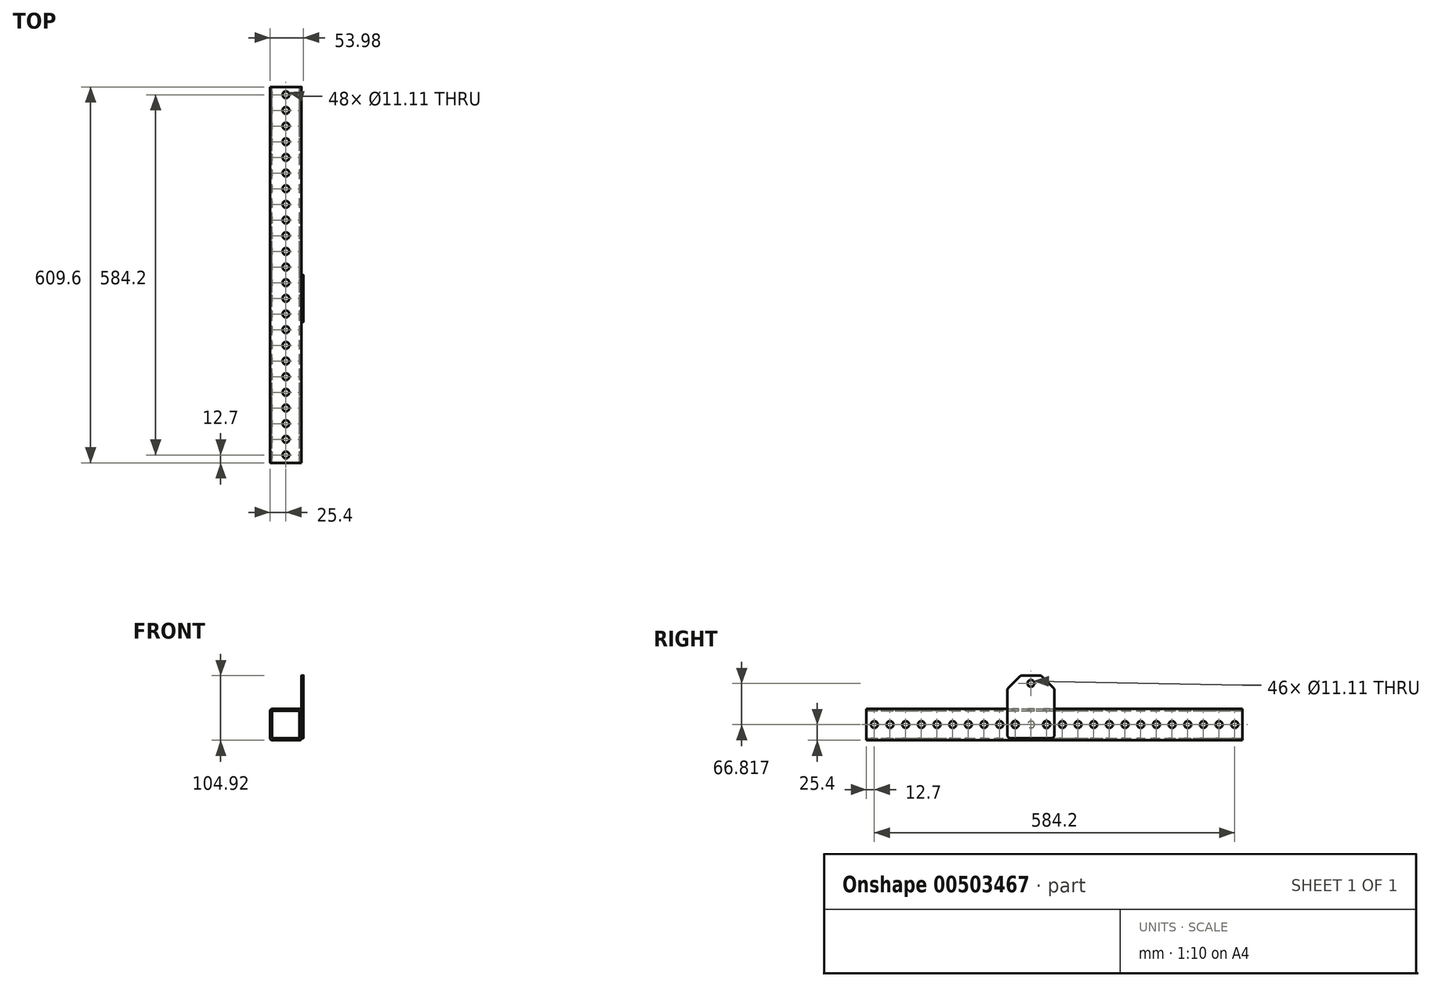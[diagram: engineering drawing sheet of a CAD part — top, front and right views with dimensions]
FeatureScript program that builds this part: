
annotation { "Feature Type Name" : "Feature", "Feature Type Description" : "" }
export const myFeature = defineFeature(function(context is Context, id is Id, definition is map)
    precondition{}
    {
        {
            var Q0;
            Q0=qCreatedBy(makeId("Front.planeOp"),FACE);
            var sketch = newSketch(context, id + "F0", { "sketchPlane" : qUnion([Q0])});
            skLineSegment(sketch, "E0.bottom", {"start": v(-3.18, 0) * mm, "end": v(-47.63, 0) * mm});
            skLineSegment(sketch, "E0.top", {"start": v(-3.17, 50.8) * mm, "end": v(-47.63, 50.8) * mm});
            skLineSegment(sketch, "E0.left", {"start": v(0, 3.18) * mm, "end": v(0, 47.63) * mm});
            skLineSegment(sketch, "E0.right", {"start": v(-50.8, 3.17) * mm, "end": v(-50.8, 47.62) * mm});
            skPoint(sketch, "E1.visualSharp", {"position": v(-50.8, 50.8) * mm});
            skArc(sketch, "E1.filletArc", {"start": v(-47.63, 50.8) * mm, "mid": v(-49.87, 49.87) * mm, "end": v(-50.8, 47.62) * mm});
            skPoint(sketch, "E2.visualSharp", {"position": v(0, 50.8) * mm});
            skArc(sketch, "E2.filletArc", {"start": v(0, 47.63) * mm, "mid": v(-0.93, 49.87) * mm, "end": v(-3.17, 50.8) * mm});
            skPoint(sketch, "E3.visualSharp", {"position": v(0, 0) * mm});
            skArc(sketch, "E3.filletArc", {"start": v(-3.18, 0) * mm, "mid": v(-0.93, 0.93) * mm, "end": v(0, 3.18) * mm});
            skPoint(sketch, "E4.visualSharp", {"position": v(-50.8, 0) * mm});
            skArc(sketch, "E4.filletArc", {"start": v(-50.8, 3.17) * mm, "mid": v(-49.87, 0.93) * mm, "end": v(-47.63, 0) * mm});
            skLineSegment(sketch, "E5.0", {"start": v(-3.18, 3.18) * mm, "end": v(-47.62, 3.17) * mm});
            skLineSegment(sketch, "E5.1", {"start": v(-3.18, 3.18) * mm, "end": v(-3.18, 47.63) * mm});
            skLineSegment(sketch, "E5.2", {"start": v(-3.18, 47.63) * mm, "end": v(-47.63, 47.62) * mm});
            skLineSegment(sketch, "E5.3", {"start": v(-47.62, 3.17) * mm, "end": v(-47.63, 47.62) * mm});
            skSolve(sketch);
        }
        {
            var Q0;
            Q0=makeQuery(id+"F0.imprint","IMPRINT",FACE,{"disambiguationData":[TD([[makeQuery(id+"F0.imprint","IMPRINT",EDGE,{"derivedFrom":sQuery(id+"F0.wireOp",EDGE,"E0.bottom")}),-1.0]])]});
            extrude(context, id + "F1", {"entities" : qUnion([Q0]), "depth" : 609.6 * mm, "offsetDistance" : 25.4 * mm, "symmetric" : true});
        }
        {
            var Q0;
            Q0=makeQuery(id+"F1.opExtrude","SWEPT_FACE",FACE,{"disambiguationData":[OSD([sQuery(id+"F0.wireOp",EDGE,"E0.right")])]});
            var sketch = newSketch(context, id + "F2", { "sketchPlane" : qUnion([Q0])});
            skLineSegment(sketch, "E6", {"start": v(-292.1, 3.17) * mm, "end": v(-292.1, 47.63) * mm, "construction": true});
            skLineSegment(sketch, "E7", {"start": v(-304.8, 25.4) * mm, "end": v(-292.1, 25.4) * mm, "construction": true});
            skCircle(sketch, "E8", {"center": v(-292.1, 25.4) * mm, "radius": 5.56 * mm});
            skCircle(sketch, "E9.1.0.0", {"center": v(-266.7, 25.4) * mm, "radius": 5.56 * mm});
            skCircle(sketch, "E9.2.0.0", {"center": v(-241.3, 25.4) * mm, "radius": 5.56 * mm});
            skCircle(sketch, "E9.3.0.0", {"center": v(-215.9, 25.4) * mm, "radius": 5.56 * mm});
            skCircle(sketch, "E9.4.0.0", {"center": v(-190.5, 25.4) * mm, "radius": 5.56 * mm});
            skCircle(sketch, "E9.5.0.0", {"center": v(-165.1, 25.4) * mm, "radius": 5.56 * mm});
            skCircle(sketch, "E9.6.0.0", {"center": v(-139.7, 25.4) * mm, "radius": 5.56 * mm});
            skCircle(sketch, "E9.7.0.0", {"center": v(-114.3, 25.4) * mm, "radius": 5.56 * mm});
            skCircle(sketch, "E9.8.0.0", {"center": v(-88.9, 25.4) * mm, "radius": 5.56 * mm});
            skCircle(sketch, "E9.9.0.0", {"center": v(-63.5, 25.4) * mm, "radius": 5.56 * mm});
            skCircle(sketch, "E9.10.0.0", {"center": v(-38.1, 25.4) * mm, "radius": 5.56 * mm});
            skCircle(sketch, "E9.11.0.0", {"center": v(-12.7, 25.4) * mm, "radius": 5.56 * mm});
            skCircle(sketch, "E9.12.0.0", {"center": v(12.7, 25.4) * mm, "radius": 5.56 * mm});
            skCircle(sketch, "E9.13.0.0", {"center": v(38.1, 25.4) * mm, "radius": 5.56 * mm});
            skCircle(sketch, "E9.14.0.0", {"center": v(63.5, 25.4) * mm, "radius": 5.56 * mm});
            skCircle(sketch, "E9.15.0.0", {"center": v(88.9, 25.4) * mm, "radius": 5.56 * mm});
            skCircle(sketch, "E9.16.0.0", {"center": v(114.3, 25.4) * mm, "radius": 5.56 * mm});
            skCircle(sketch, "E9.17.0.0", {"center": v(139.7, 25.4) * mm, "radius": 5.56 * mm});
            skCircle(sketch, "E9.18.0.0", {"center": v(165.1, 25.4) * mm, "radius": 5.56 * mm});
            skCircle(sketch, "E9.19.0.0", {"center": v(190.5, 25.4) * mm, "radius": 5.56 * mm});
            skCircle(sketch, "E9.20.0.0", {"center": v(215.9, 25.4) * mm, "radius": 5.56 * mm});
            skCircle(sketch, "E9.21.0.0", {"center": v(241.3, 25.4) * mm, "radius": 5.56 * mm});
            skCircle(sketch, "E9.22.0.0", {"center": v(266.7, 25.4) * mm, "radius": 5.56 * mm});
            skCircle(sketch, "E9.23.0.0", {"center": v(292.1, 25.4) * mm, "radius": 5.56 * mm});
            skLineSegment(sketch, "E9.direction1", {"start": v(-292.1, 25.4) * mm, "end": v(-266.7, 25.4) * mm, "construction": true});
            skSolve(sketch);
        }
        {
            var Q0;
            Q0 = qSketchRegion(id + "F2", true);
            extrude(context, id + "F3", {"entities" : qUnion([Q0]), "operationType" : NewBodyOperationType.REMOVE, "oppositeDirection" : true, "depth" : 50.8 * mm, "offsetDistance" : 25.4 * mm});
        }
        {
            var Q0;
            Q0=makeQuery(id+"F1.opExtrude","SWEPT_FACE",FACE,{"disambiguationData":[OSD([sQuery(id+"F0.wireOp",EDGE,"E0.top")])]});
            var sketch = newSketch(context, id + "F4", { "sketchPlane" : qUnion([Q0])});
            skCircle(sketch, "E10", {"center": v(-25.4, 292.1) * mm, "radius": 5.56 * mm});
            skPoint(sketch, "E10.centerSnap0", {"position": v(-25.4, 304.8) * mm});
            skCircle(sketch, "E11.0.1.0", {"center": v(-25.4, 266.7) * mm, "radius": 5.56 * mm});
            skCircle(sketch, "E11.0.2.0", {"center": v(-25.4, 241.3) * mm, "radius": 5.56 * mm});
            skCircle(sketch, "E11.0.3.0", {"center": v(-25.4, 215.9) * mm, "radius": 5.56 * mm});
            skCircle(sketch, "E11.0.4.0", {"center": v(-25.4, 190.5) * mm, "radius": 5.56 * mm});
            skCircle(sketch, "E11.0.5.0", {"center": v(-25.4, 165.1) * mm, "radius": 5.56 * mm});
            skCircle(sketch, "E11.0.6.0", {"center": v(-25.4, 139.7) * mm, "radius": 5.56 * mm});
            skCircle(sketch, "E11.0.7.0", {"center": v(-25.4, 114.3) * mm, "radius": 5.56 * mm});
            skCircle(sketch, "E11.0.8.0", {"center": v(-25.4, 88.9) * mm, "radius": 5.56 * mm});
            skCircle(sketch, "E11.0.9.0", {"center": v(-25.4, 63.5) * mm, "radius": 5.56 * mm});
            skCircle(sketch, "E11.0.10.0", {"center": v(-25.4, 38.1) * mm, "radius": 5.56 * mm});
            skCircle(sketch, "E11.0.11.0", {"center": v(-25.4, 12.7) * mm, "radius": 5.56 * mm});
            skCircle(sketch, "E11.0.12.0", {"center": v(-25.4, -12.7) * mm, "radius": 5.56 * mm});
            skCircle(sketch, "E11.0.13.0", {"center": v(-25.4, -38.1) * mm, "radius": 5.56 * mm});
            skCircle(sketch, "E11.0.14.0", {"center": v(-25.4, -63.5) * mm, "radius": 5.56 * mm});
            skCircle(sketch, "E11.0.15.0", {"center": v(-25.4, -88.9) * mm, "radius": 5.56 * mm});
            skCircle(sketch, "E11.0.16.0", {"center": v(-25.4, -114.3) * mm, "radius": 5.56 * mm});
            skCircle(sketch, "E11.0.17.0", {"center": v(-25.4, -139.7) * mm, "radius": 5.56 * mm});
            skCircle(sketch, "E11.0.18.0", {"center": v(-25.4, -165.1) * mm, "radius": 5.56 * mm});
            skCircle(sketch, "E11.0.19.0", {"center": v(-25.4, -190.5) * mm, "radius": 5.56 * mm});
            skCircle(sketch, "E11.0.20.0", {"center": v(-25.4, -215.9) * mm, "radius": 5.56 * mm});
            skCircle(sketch, "E11.0.21.0", {"center": v(-25.4, -241.3) * mm, "radius": 5.56 * mm});
            skCircle(sketch, "E11.0.22.0", {"center": v(-25.4, -266.7) * mm, "radius": 5.56 * mm});
            skCircle(sketch, "E11.0.23.0", {"center": v(-25.4, -292.1) * mm, "radius": 5.56 * mm});
            skLineSegment(sketch, "E11.direction1", {"start": v(-25.4, 292.1) * mm, "end": v(0, 292.1) * mm, "construction": true});
            skLineSegment(sketch, "E11.direction2", {"start": v(-25.4, 292.1) * mm, "end": v(-25.4, 266.7) * mm, "construction": true});
            skSolve(sketch);
        }
        {
            var Q0;
            Q0=makeQuery(id+"F4.imprint","IMPRINT",FACE,{"disambiguationData":[TD([[makeQuery(id+"F4.imprint","IMPRINT",EDGE,{"derivedFrom":sQuery(id+"F4.wireOp",EDGE,"E11.0.23.0")}),1.0]])]});
            var Q1;
            Q1=makeQuery(id+"F4.imprint","IMPRINT",FACE,{"disambiguationData":[TD([[makeQuery(id+"F4.imprint","IMPRINT",EDGE,{"derivedFrom":sQuery(id+"F4.wireOp",EDGE,"E11.0.22.0")}),1.0]])]});
            var Q2;
            Q2=makeQuery(id+"F4.imprint","IMPRINT",FACE,{"disambiguationData":[TD([[makeQuery(id+"F4.imprint","IMPRINT",EDGE,{"derivedFrom":sQuery(id+"F4.wireOp",EDGE,"E11.0.21.0")}),1.0]])]});
            var Q3;
            Q3=makeQuery(id+"F4.imprint","IMPRINT",FACE,{"disambiguationData":[TD([[makeQuery(id+"F4.imprint","IMPRINT",EDGE,{"derivedFrom":sQuery(id+"F4.wireOp",EDGE,"E11.0.20.0")}),1.0]])]});
            var Q4;
            Q4=makeQuery(id+"F4.imprint","IMPRINT",FACE,{"disambiguationData":[TD([[makeQuery(id+"F4.imprint","IMPRINT",EDGE,{"derivedFrom":sQuery(id+"F4.wireOp",EDGE,"E11.0.19.0")}),1.0]])]});
            var Q5;
            Q5=makeQuery(id+"F4.imprint","IMPRINT",FACE,{"disambiguationData":[TD([[makeQuery(id+"F4.imprint","IMPRINT",EDGE,{"derivedFrom":sQuery(id+"F4.wireOp",EDGE,"E11.0.18.0")}),1.0]])]});
            var Q6;
            Q6=makeQuery(id+"F4.imprint","IMPRINT",FACE,{"disambiguationData":[TD([[makeQuery(id+"F4.imprint","IMPRINT",EDGE,{"derivedFrom":sQuery(id+"F4.wireOp",EDGE,"E11.0.17.0")}),1.0]])]});
            var Q7;
            Q7=makeQuery(id+"F4.imprint","IMPRINT",FACE,{"disambiguationData":[TD([[makeQuery(id+"F4.imprint","IMPRINT",EDGE,{"derivedFrom":sQuery(id+"F4.wireOp",EDGE,"E11.0.16.0")}),1.0]])]});
            var Q8;
            Q8=makeQuery(id+"F4.imprint","IMPRINT",FACE,{"disambiguationData":[TD([[makeQuery(id+"F4.imprint","IMPRINT",EDGE,{"derivedFrom":sQuery(id+"F4.wireOp",EDGE,"E11.0.15.0")}),1.0]])]});
            var Q9;
            Q9=makeQuery(id+"F4.imprint","IMPRINT",FACE,{"disambiguationData":[TD([[makeQuery(id+"F4.imprint","IMPRINT",EDGE,{"derivedFrom":sQuery(id+"F4.wireOp",EDGE,"E11.0.14.0")}),1.0]])]});
            var Q10;
            Q10=makeQuery(id+"F4.imprint","IMPRINT",FACE,{"disambiguationData":[TD([[makeQuery(id+"F4.imprint","IMPRINT",EDGE,{"derivedFrom":sQuery(id+"F4.wireOp",EDGE,"E11.0.13.0")}),1.0]])]});
            var Q11;
            Q11=makeQuery(id+"F4.imprint","IMPRINT",FACE,{"disambiguationData":[TD([[makeQuery(id+"F4.imprint","IMPRINT",EDGE,{"derivedFrom":sQuery(id+"F4.wireOp",EDGE,"E11.0.12.0")}),1.0]])]});
            var Q12;
            Q12=makeQuery(id+"F4.imprint","IMPRINT",FACE,{"disambiguationData":[TD([[makeQuery(id+"F4.imprint","IMPRINT",EDGE,{"derivedFrom":sQuery(id+"F4.wireOp",EDGE,"E11.0.11.0")}),1.0]])]});
            var Q13;
            Q13=makeQuery(id+"F4.imprint","IMPRINT",FACE,{"disambiguationData":[TD([[makeQuery(id+"F4.imprint","IMPRINT",EDGE,{"derivedFrom":sQuery(id+"F4.wireOp",EDGE,"E11.0.10.0")}),1.0]])]});
            var Q14;
            Q14=makeQuery(id+"F4.imprint","IMPRINT",FACE,{"disambiguationData":[TD([[makeQuery(id+"F4.imprint","IMPRINT",EDGE,{"derivedFrom":sQuery(id+"F4.wireOp",EDGE,"E11.0.9.0")}),1.0]])]});
            var Q15;
            Q15=makeQuery(id+"F4.imprint","IMPRINT",FACE,{"disambiguationData":[TD([[makeQuery(id+"F4.imprint","IMPRINT",EDGE,{"derivedFrom":sQuery(id+"F4.wireOp",EDGE,"E11.0.8.0")}),1.0]])]});
            var Q16;
            Q16=makeQuery(id+"F4.imprint","IMPRINT",FACE,{"disambiguationData":[TD([[makeQuery(id+"F4.imprint","IMPRINT",EDGE,{"derivedFrom":sQuery(id+"F4.wireOp",EDGE,"E11.0.7.0")}),1.0]])]});
            var Q17;
            Q17=makeQuery(id+"F4.imprint","IMPRINT",FACE,{"disambiguationData":[TD([[makeQuery(id+"F4.imprint","IMPRINT",EDGE,{"derivedFrom":sQuery(id+"F4.wireOp",EDGE,"E11.0.6.0")}),1.0]])]});
            var Q18;
            Q18=makeQuery(id+"F4.imprint","IMPRINT",FACE,{"disambiguationData":[TD([[makeQuery(id+"F4.imprint","IMPRINT",EDGE,{"derivedFrom":sQuery(id+"F4.wireOp",EDGE,"E11.0.5.0")}),1.0]])]});
            var Q19;
            Q19=makeQuery(id+"F4.imprint","IMPRINT",FACE,{"disambiguationData":[TD([[makeQuery(id+"F4.imprint","IMPRINT",EDGE,{"derivedFrom":sQuery(id+"F4.wireOp",EDGE,"E11.0.4.0")}),1.0]])]});
            var Q20;
            Q20=makeQuery(id+"F4.imprint","IMPRINT",FACE,{"disambiguationData":[TD([[makeQuery(id+"F4.imprint","IMPRINT",EDGE,{"derivedFrom":sQuery(id+"F4.wireOp",EDGE,"E11.0.3.0")}),1.0]])]});
            var Q21;
            Q21=makeQuery(id+"F4.imprint","IMPRINT",FACE,{"disambiguationData":[TD([[makeQuery(id+"F4.imprint","IMPRINT",EDGE,{"derivedFrom":sQuery(id+"F4.wireOp",EDGE,"E11.0.2.0")}),1.0]])]});
            var Q22;
            Q22=makeQuery(id+"F4.imprint","IMPRINT",FACE,{"disambiguationData":[TD([[makeQuery(id+"F4.imprint","IMPRINT",EDGE,{"derivedFrom":sQuery(id+"F4.wireOp",EDGE,"E11.0.1.0")}),1.0]])]});
            var Q23;
            Q23=makeQuery(id+"F4.imprint","IMPRINT",FACE,{"disambiguationData":[TD([[makeQuery(id+"F4.imprint","IMPRINT",EDGE,{"derivedFrom":sQuery(id+"F4.wireOp",EDGE,"E10")}),1.0]])]});
            extrude(context, id + "F5", {"entities" : qUnion([Q0, Q1, Q2, Q3, Q4, Q5, Q6, Q7, Q8, Q9, Q10, Q11, Q12, Q13, Q14, Q15, Q16, Q17, Q18, Q19, Q20, Q21, Q22, Q23]), "operationType" : NewBodyOperationType.REMOVE, "oppositeDirection" : true, "depth" : 50.8 * mm, "offsetDistance" : 25.4 * mm});
        }
        {
            var Q0;
            Q0=qCreatedBy(makeId("Right.planeOp"),FACE);
            var sketch = newSketch(context, id + "F6", { "sketchPlane" : qUnion([Q0])});
            skLineSegment(sketch, "E12", {"start": v(-12.94, 25.54) * mm, "end": v(12.46, 25.54) * mm, "construction": true});
            skLineSegment(sketch, "E13", {"start": v(-38.34, 3.32) * mm, "end": v(-0.24, 3.32) * mm});
            skLineSegment(sketch, "E14", {"start": v(-0.24, 3.32) * mm, "end": v(-0.24, 83.2) * mm});
            skLineSegment(sketch, "E15", {"start": v(-38.34, 104.92) * mm, "end": v(-21.97, 104.92) * mm});
            skLineSegment(sketch, "E16", {"start": v(-0.24, 83.2) * mm, "end": v(-21.97, 104.92) * mm});
            skPoint(sketch, "E17", {"position": v(-21.97, 104.92) * mm});
            skLineSegment(sketch, "E18", {"start": v(-38.34, 3.32) * mm, "end": v(-38.34, 104.92) * mm, "construction": true});
            skPoint(sketch, "E19", {"position": v(-12.94, 25.54) * mm});
            skLineSegment(sketch, "E20.MirrorCS", {"start": v(-38.34, 104.92) * mm, "end": v(-54.72, 104.92) * mm});
            skLineSegment(sketch, "E21.MirrorCS", {"start": v(-76.44, 83.2) * mm, "end": v(-54.72, 104.92) * mm});
            skLineSegment(sketch, "E22.MirrorCS", {"start": v(-76.44, 3.32) * mm, "end": v(-76.44, 83.2) * mm});
            skLineSegment(sketch, "E23.MirrorCS", {"start": v(-38.34, 3.32) * mm, "end": v(-76.44, 3.32) * mm});
            skCircle(sketch, "E24", {"center": v(-12.94, 25.54) * mm, "radius": 5.77 * mm});
            skCircle(sketch, "E25.MirrorC", {"center": v(-63.74, 25.54) * mm, "radius": 5.77 * mm});
            skCircle(sketch, "E26", {"center": v(-38.34, 92.22) * mm, "radius": 5.56 * mm});
            skSolve(sketch);
        }
        {
            var Q0;
            Q0=makeQuery(id+"F6.imprint","IMPRINT",FACE,{"disambiguationData":[TD([[makeQuery(id+"F6.imprint","IMPRINT",EDGE,{"derivedFrom":sQuery(id+"F6.wireOp",EDGE,"E13")}),1.0]])]});
            extrude(context, id + "F7", {"entities" : qUnion([Q0]), "operationType" : NewBodyOperationType.ADD, "depth" : 3.17 * mm, "offsetDistance" : 25.4 * mm});
        }
        {
            var Q0;
            Q0=makeQuery(id+"F7.opExtrude","SWEPT_EDGE",EDGE,{"disambiguationData":[OSD([sQuery(id+"F6.wireOp",EDGE,"E22.MirrorCS"),sQuery(id+"F6.wireOp",EDGE,"E23.MirrorCS")])]});
            var Q1;
            Q1=makeQuery(id+"F7.opExtrude","SWEPT_EDGE",EDGE,{"disambiguationData":[OSD([sQuery(id+"F6.wireOp",EDGE,"E21.MirrorCS"),sQuery(id+"F6.wireOp",EDGE,"E22.MirrorCS")])]});
            var Q2;
            Q2=makeQuery(id+"F7.opExtrude","SWEPT_EDGE",EDGE,{"disambiguationData":[OSD([sQuery(id+"F6.wireOp",EDGE,"E20.MirrorCS"),sQuery(id+"F6.wireOp",EDGE,"E21.MirrorCS")])]});
            var Q3;
            Q3=makeQuery(id+"F7.opExtrude","SWEPT_EDGE",EDGE,{"disambiguationData":[OSD([sQuery(id+"F6.wireOp",EDGE,"E14"),sQuery(id+"F6.wireOp",EDGE,"E16")])]});
            var Q4;
            Q4=makeQuery(id+"F7.opExtrude","SWEPT_EDGE",EDGE,{"disambiguationData":[OSD([sQuery(id+"F6.wireOp",EDGE,"E15"),sQuery(id+"F6.wireOp",EDGE,"E16")])]});
            var Q5;
            Q5=makeQuery(id+"F7.opExtrude","SWEPT_EDGE",EDGE,{"disambiguationData":[OSD([sQuery(id+"F6.wireOp",EDGE,"E13"),sQuery(id+"F6.wireOp",EDGE,"E14")])]});
            fillet(context, id + "F8", {"entities" : qUnion([Q0, Q1, Q2, Q3, Q4, Q5]), "radius" : 5.08 * mm, "tangentPropagation" : true, "allowEdgeOverflow" : false});
        }
    });
